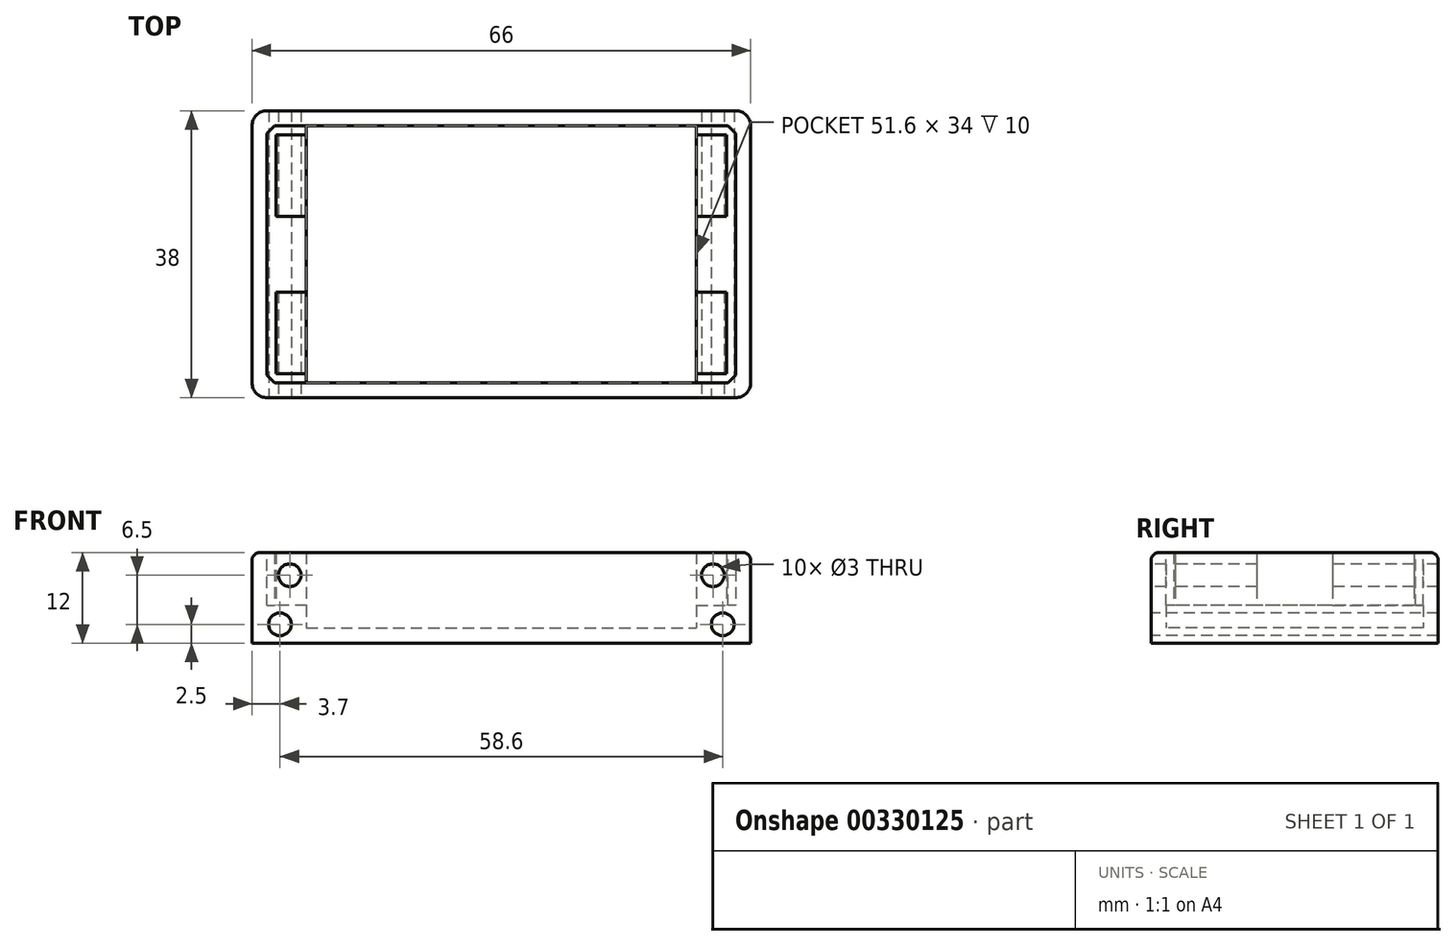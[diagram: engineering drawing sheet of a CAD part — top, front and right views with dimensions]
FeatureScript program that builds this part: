
annotation { "Feature Type Name" : "Feature", "Feature Type Description" : "" }
export const myFeature = defineFeature(function(context is Context, id is Id, definition is map)
    precondition{}
    {
        {
            var Q0;
            Q0=qCreatedBy(makeId("Top.planeOp"),FACE);
            var sketch = newSketch(context, id + "F0", { "sketchPlane" : qUnion([Q0])});
            skLineSegment(sketch, "E0.bottom", {"start": v(0, 0) * mm, "end": v(66, 0) * mm});
            skLineSegment(sketch, "E0.top", {"start": v(0, -38) * mm, "end": v(66, -38) * mm});
            skLineSegment(sketch, "E0.left", {"start": v(0, 0) * mm, "end": v(0, -38) * mm});
            skLineSegment(sketch, "E0.right", {"start": v(66, 0) * mm, "end": v(66, -38) * mm});
            skSolve(sketch);
        }
        {
            var Q0;
            Q0=qSketchRegion(id+"F0",true);
            extrude(context, id + "F1", {"entities" : qUnion([Q0]), "depth" : 2 * mm});
        }
        {
            var Q0;
            Q0=makeQuery(id+"F1.opExtrude","CAP_FACE",FACE,{"disambiguationData":[OSD([sQuery(id+"F0.wireOp",EDGE,"E0.bottom"),sQuery(id+"F0.wireOp",EDGE,"E0.top"),sQuery(id+"F0.wireOp",EDGE,"E0.left"),sQuery(id+"F0.wireOp",EDGE,"E0.right")])],"isStart":false});
            var sketch = newSketch(context, id + "F2", { "sketchPlane" : qUnion([Q0])});
            skLineSegment(sketch, "E1.bottom", {"start": v(2, -2) * mm, "end": v(64, -2) * mm});
            skLineSegment(sketch, "E1.top", {"start": v(2, -36) * mm, "end": v(64, -36) * mm});
            skLineSegment(sketch, "E1.left", {"start": v(2, -2) * mm, "end": v(2, -36) * mm});
            skLineSegment(sketch, "E1.right", {"start": v(64, -2) * mm, "end": v(64, -36) * mm});
            skSolve(sketch);
        }
        {
            var Q0;
            Q0=makeQuery(id+"F2.imprint","IMPRINT",FACE,{"disambiguationData":[TD([[makeQuery(id+"F2.imprint","IMPRINT",EDGE,{"derivedFrom":sQuery(id+"F2.wireOp",EDGE,"E1.bottom")}),1.0]])]});
            extrude(context, id + "F3", {"entities" : qUnion([Q0]), "operationType" : NewBodyOperationType.ADD, "depth" : 10 * mm});
        }
        {
            var Q0;
            Q0=makeQuery(id+"F3.opExtrude","SWEPT_EDGE",EDGE,{"disambiguationData":[OSD([sQuery(id+"F2.wireOp",EDGE,"E1.bottom"),sQuery(id+"F2.wireOp",EDGE,"E1.left")])]});
            var Q1;
            Q1=makeQuery(id+"F3.opExtrude","SWEPT_EDGE",EDGE,{"disambiguationData":[OSD([sQuery(id+"F2.wireOp",EDGE,"E1.top"),sQuery(id+"F2.wireOp",EDGE,"E1.left")])]});
            var Q2;
            Q2=makeQuery(id+"F3.opExtrude","SWEPT_EDGE",EDGE,{"disambiguationData":[OSD([sQuery(id+"F2.wireOp",EDGE,"E1.bottom"),sQuery(id+"F2.wireOp",EDGE,"E1.right")])]});
            var Q3;
            Q3=makeQuery(id+"F3.opExtrude","SWEPT_EDGE",EDGE,{"disambiguationData":[OSD([sQuery(id+"F2.wireOp",EDGE,"E1.top"),sQuery(id+"F2.wireOp",EDGE,"E1.right")])]});
            chamfer(context, id + "F4", {"entities" : qUnion([Q0, Q1, Q2, Q3]), "width" : 1 * mm, "tangentPropagation" : true});
        }
        {
            var Q0;
            {var subQ0=sQuery(id+"F0.wireOp",EDGE,"E0.left");var subQ1=sQuery(id+"F0.wireOp",EDGE,"E0.top");Q0=makeQuery(id+"F3.boolean.opBoolean","MERGE",EDGE,{"derivedFrom":[makeQuery(id+"F1.opExtrude","SWEPT_EDGE",EDGE,{"disambiguationData":[OSD([subQ1,subQ0])]}),makeQuery(id+"F3.opExtrude","SWEPT_EDGE",EDGE,{"disambiguationData":[OSD([subQ1,subQ0])]})]});}
            var Q1;
            {var subQ0=sQuery(id+"F0.wireOp",EDGE,"E0.right");var subQ1=sQuery(id+"F0.wireOp",EDGE,"E0.top");Q1=makeQuery(id+"F3.boolean.opBoolean","MERGE",EDGE,{"derivedFrom":[makeQuery(id+"F1.opExtrude","SWEPT_EDGE",EDGE,{"disambiguationData":[OSD([subQ1,subQ0])]}),makeQuery(id+"F3.opExtrude","SWEPT_EDGE",EDGE,{"disambiguationData":[OSD([subQ1,subQ0])]})]});}
            var Q2;
            {var subQ0=sQuery(id+"F0.wireOp",EDGE,"E0.right");var subQ1=sQuery(id+"F0.wireOp",EDGE,"E0.bottom");Q2=makeQuery(id+"F3.boolean.opBoolean","MERGE",EDGE,{"derivedFrom":[makeQuery(id+"F1.opExtrude","SWEPT_EDGE",EDGE,{"disambiguationData":[OSD([subQ1,subQ0])]}),makeQuery(id+"F3.opExtrude","SWEPT_EDGE",EDGE,{"disambiguationData":[OSD([subQ1,subQ0])]})]});}
            var Q3;
            {var subQ0=sQuery(id+"F0.wireOp",EDGE,"E0.left");var subQ1=sQuery(id+"F0.wireOp",EDGE,"E0.bottom");Q3=makeQuery(id+"F3.boolean.opBoolean","MERGE",EDGE,{"derivedFrom":[makeQuery(id+"F1.opExtrude","SWEPT_EDGE",EDGE,{"disambiguationData":[OSD([subQ1,subQ0])]}),makeQuery(id+"F3.opExtrude","SWEPT_EDGE",EDGE,{"disambiguationData":[OSD([subQ1,subQ0])]})]});}
            fillet(context, id + "F5", {"entities" : qUnion([Q0, Q1, Q2, Q3]), "radius" : 2 * mm, "tangentPropagation" : true, "allowEdgeOverflow" : false});
        }
        {
            var Q0;
            Q0=makeQuery(id+"F3.opExtrude","CAP_EDGE",EDGE,{"disambiguationData":[OSD([sQuery(id+"F0.wireOp",EDGE,"E0.left")])],"isStart":false});
            var Q1;
            Q1=makeQuery(id+"F3.opExtrude","CAP_EDGE",EDGE,{"disambiguationData":[OSD([sQuery(id+"F0.wireOp",EDGE,"E0.top")])],"isStart":false});
            var Q2;
            Q2=makeQuery(id+"F3.opExtrude","CAP_EDGE",EDGE,{"disambiguationData":[OSD([sQuery(id+"F0.wireOp",EDGE,"E0.right")])],"isStart":false});
            var Q3;
            Q3=makeQuery(id+"F3.opExtrude","CAP_EDGE",EDGE,{"disambiguationData":[OSD([sQuery(id+"F0.wireOp",EDGE,"E0.bottom")])],"isStart":false});
            fillet(context, id + "F6", {"entities" : qUnion([Q0, Q1, Q2, Q3]), "radius" : 1 * mm, "tangentPropagation" : true, "allowEdgeOverflow" : false});
        }
        {
            var Q0;
            Q0=makeQuery(id+"F1.opExtrude","CAP_FACE",FACE,{"disambiguationData":[OSD([sQuery(id+"F0.wireOp",EDGE,"E0.bottom"),sQuery(id+"F0.wireOp",EDGE,"E0.top"),sQuery(id+"F0.wireOp",EDGE,"E0.left"),sQuery(id+"F0.wireOp",EDGE,"E0.right")])],"isStart":false});
            var sketch = newSketch(context, id + "F7", { "sketchPlane" : qUnion([Q0])});
            skLineSegment(sketch, "E2.bottom", {"start": v(7.2, -2) * mm, "end": v(2, -2) * mm});
            skLineSegment(sketch, "E2.top", {"start": v(7.2, -36) * mm, "end": v(2, -36) * mm});
            skLineSegment(sketch, "E2.left", {"start": v(7.2, -2) * mm, "end": v(7.2, -36) * mm});
            skLineSegment(sketch, "E2.right", {"start": v(2, -2) * mm, "end": v(2, -36) * mm});
            skLineSegment(sketch, "E3.bottom", {"start": v(58.8, -2) * mm, "end": v(64, -2) * mm});
            skLineSegment(sketch, "E3.top", {"start": v(58.8, -36) * mm, "end": v(64, -36) * mm});
            skLineSegment(sketch, "E3.left", {"start": v(58.8, -2) * mm, "end": v(58.8, -36) * mm});
            skLineSegment(sketch, "E3.right", {"start": v(64, -2) * mm, "end": v(64, -36) * mm});
            skSolve(sketch);
        }
        {
            var Q0;
            Q0=qSketchRegion(id+"F7",true);
            extrude(context, id + "F8", {"entities" : qUnion([Q0]), "operationType" : NewBodyOperationType.ADD, "depth" : 3 * mm});
        }
        {
            var Q0;
            {var subQ0=sQuery(id+"F0.wireOp",EDGE,"E0.top");Q0=makeQuery(id+"F3.boolean.opBoolean","MERGE",FACE,{"derivedFrom":[makeQuery(id+"F1.opExtrude","SWEPT_FACE",FACE,{"disambiguationData":[OSD([subQ0])]}),makeQuery(id+"F3.opExtrude","SWEPT_FACE",FACE,{"disambiguationData":[OSD([subQ0])]})]});}
            var sketch = newSketch(context, id + "F9", { "sketchPlane" : qUnion([Q0])});
            skCircle(sketch, "E4", {"center": v(3.7, 2.5) * mm, "radius": 1.5 * mm});
            skCircle(sketch, "E5", {"center": v(62.3, 2.5) * mm, "radius": 1.5 * mm});
            skSolve(sketch);
        }
        {
            var Q0;
            Q0=qSketchRegion(id+"F9",true);
            extrude(context, id + "F10", {"entities" : qUnion([Q0]), "operationType" : NewBodyOperationType.REMOVE, "endBound" : BoundingType.THROUGH_ALL, "oppositeDirection" : true, "depth" : 25 * mm});
        }
        {
            var Q0;
            Q0=makeQuery(id+"F8.opExtrude","CAP_FACE",FACE,{"disambiguationData":[OSD([sQuery(id+"F7.wireOp",EDGE,"E2.bottom"),sQuery(id+"F7.wireOp",EDGE,"E2.top"),sQuery(id+"F7.wireOp",EDGE,"E2.left"),sQuery(id+"F7.wireOp",EDGE,"E2.right")])],"isStart":false});
            var sketch = newSketch(context, id + "F11", { "sketchPlane" : qUnion([Q0])});
            skLineSegment(sketch, "E6.bottom", {"start": v(7.2, -14) * mm, "end": v(3.2, -14) * mm});
            skLineSegment(sketch, "E6.top", {"start": v(7.2, -3.2) * mm, "end": v(3.2, -3.2) * mm});
            skLineSegment(sketch, "E6.left", {"start": v(7.2, -14) * mm, "end": v(7.2, -3.2) * mm});
            skLineSegment(sketch, "E6.right", {"start": v(3.2, -14) * mm, "end": v(3.2, -3.2) * mm});
            skLineSegment(sketch, "E7.bottom", {"start": v(7.2, -24) * mm, "end": v(3.2, -24) * mm});
            skLineSegment(sketch, "E7.top", {"start": v(7.2, -34.8) * mm, "end": v(3.2, -34.8) * mm});
            skLineSegment(sketch, "E7.left", {"start": v(7.2, -24) * mm, "end": v(7.2, -34.8) * mm});
            skLineSegment(sketch, "E7.right", {"start": v(3.2, -24) * mm, "end": v(3.2, -34.8) * mm});
            skLineSegment(sketch, "E8.bottom", {"start": v(58.8, -3.2) * mm, "end": v(62.8, -3.2) * mm});
            skLineSegment(sketch, "E8.top", {"start": v(58.8, -14) * mm, "end": v(62.8, -14) * mm});
            skLineSegment(sketch, "E8.left", {"start": v(58.8, -3.2) * mm, "end": v(58.8, -14) * mm});
            skLineSegment(sketch, "E8.right", {"start": v(62.8, -3.2) * mm, "end": v(62.8, -14) * mm});
            skLineSegment(sketch, "E9.bottom", {"start": v(58.8, -24) * mm, "end": v(62.8, -24) * mm});
            skLineSegment(sketch, "E9.top", {"start": v(58.8, -34.8) * mm, "end": v(62.8, -34.8) * mm});
            skLineSegment(sketch, "E9.left", {"start": v(58.8, -24) * mm, "end": v(58.8, -34.8) * mm});
            skLineSegment(sketch, "E9.right", {"start": v(62.8, -24) * mm, "end": v(62.8, -34.8) * mm});
            skSolve(sketch);
        }
        {
            var Q0;
            Q0=qSketchRegion(id+"F11",true);
            extrude(context, id + "F12", {"entities" : qUnion([Q0]), "operationType" : NewBodyOperationType.ADD, "depth" : 7 * mm});
        }
        {
            var Q0;
            {var subQ0=sQuery(id+"F0.wireOp",EDGE,"E0.top");Q0=makeQuery(id+"F3.boolean.opBoolean","MERGE",FACE,{"derivedFrom":[makeQuery(id+"F1.opExtrude","SWEPT_FACE",FACE,{"disambiguationData":[OSD([subQ0])]}),makeQuery(id+"F3.opExtrude","SWEPT_FACE",FACE,{"disambiguationData":[OSD([subQ0])]})]});}
            var sketch = newSketch(context, id + "F13", { "sketchPlane" : qUnion([Q0])});
            skCircle(sketch, "E10", {"center": v(5, 9) * mm, "radius": 1.5 * mm});
            skCircle(sketch, "E11", {"center": v(61, 9) * mm, "radius": 1.5 * mm});
            skSolve(sketch);
        }
        {
            var Q0;
            Q0=qSketchRegion(id+"F13",true);
            extrude(context, id + "F14", {"entities" : qUnion([Q0]), "operationType" : NewBodyOperationType.REMOVE, "endBound" : BoundingType.THROUGH_ALL, "oppositeDirection" : true, "depth" : 25 * mm});
        }
    });
